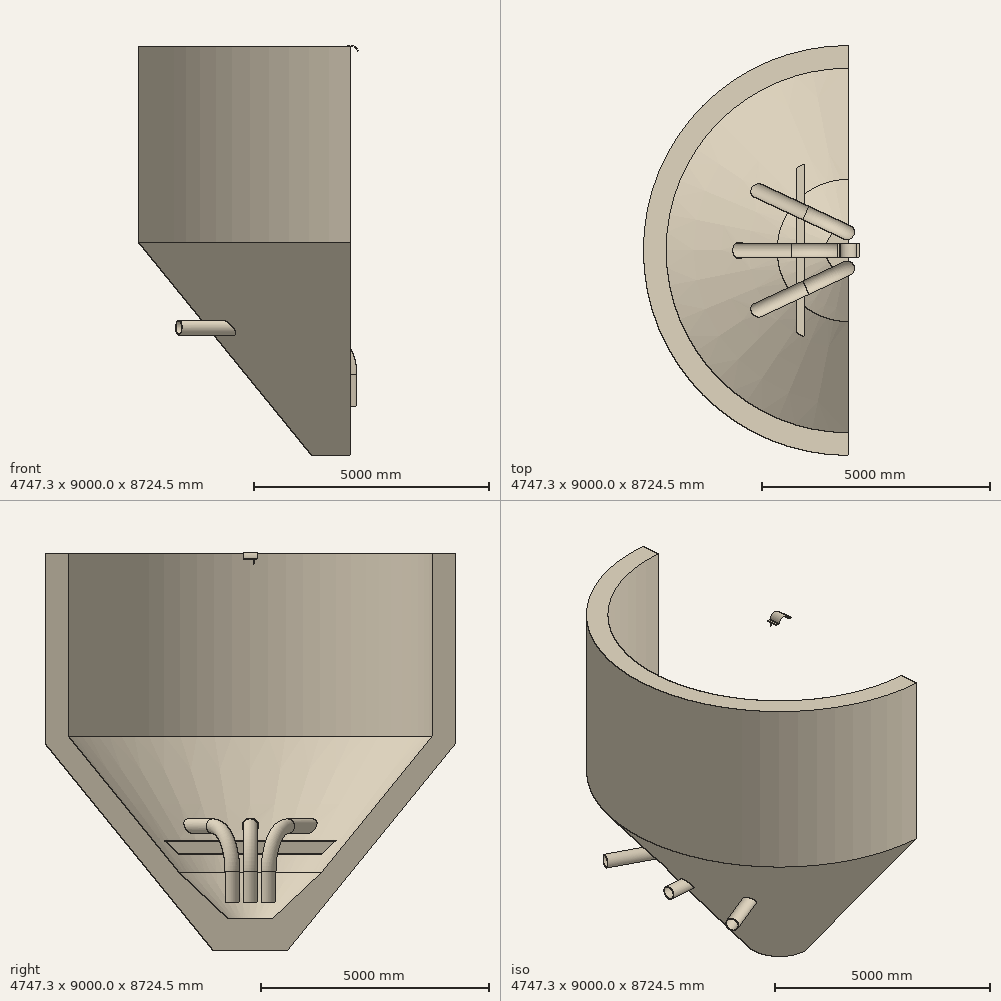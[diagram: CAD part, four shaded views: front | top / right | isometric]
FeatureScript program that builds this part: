
annotation { "Feature Type Name" : "Feature", "Feature Type Description" : "" }
export const myFeature = defineFeature(function(context is Context, id is Id, definition is map)
    precondition{}
    {
        {
            var Q0;
            Q0=qCreatedBy(makeId("Front.planeOp"),FACE);
            var sketch = newSketch(context, id + "F0", { "sketchPlane" : qUnion([Q0])});
            skLineSegment(sketch, "E0", {"start": v(-119.04, 0) * mm, "end": v(208.1, 0) * mm, "construction": true});
            skArc(sketch, "E1", {"start": v(164.9, -41.35) * mm, "mid": v(104.57, -134.03) * mm, "end": v(0, -170) * mm});
            skLineSegment(sketch, "E2", {"start": v(179.44, -30) * mm, "end": v(247.33, -30) * mm});
            skLineSegment(sketch, "E3", {"start": v(0, 1013.15) * mm, "end": v(0, 0) * mm, "construction": true});
            skArc(sketch, "E4.0", {"start": v(171.16, -48.88) * mm, "mid": v(165.4, -65.76) * mm, "end": v(158, -81.98) * mm});
            skLineSegment(sketch, "E5", {"start": v(185.58, -38) * mm, "end": v(247.33, -38) * mm});
            skLineSegment(sketch, "E6", {"start": v(247.33, -30) * mm, "end": v(247.33, -38) * mm});
            skPoint(sketch, "E7.visualSharp", {"position": v(167.33, -30) * mm});
            skArc(sketch, "E7.filletArc", {"start": v(179.44, -30) * mm, "mid": v(170.22, -33.17) * mm, "end": v(164.9, -41.35) * mm});
            skPoint(sketch, "E8.visualSharp", {"position": v(173.9, -38) * mm});
            skArc(sketch, "E8.filletArc", {"start": v(185.58, -38) * mm, "mid": v(176.55, -41.03) * mm, "end": v(171.16, -48.88) * mm});
            skLineSegment(sketch, "E9.MirrorCS", {"start": v(-247.33, -30) * mm, "end": v(-247.33, -38) * mm});
            skArc(sketch, "E10.MirrorCS", {"start": v(-185.58, -38) * mm, "mid": v(-176.55, -41.03) * mm, "end": v(-171.16, -48.88) * mm});
            skArc(sketch, "E11.MirrorCS", {"start": v(-179.44, -30) * mm, "mid": v(-170.22, -33.17) * mm, "end": v(-164.9, -41.35) * mm});
            skArc(sketch, "E12.MirrorCS", {"start": v(-171.16, -48.88) * mm, "mid": v(-165.4, -65.76) * mm, "end": v(-158, -81.98) * mm});
            skLineSegment(sketch, "E13.MirrorCS", {"start": v(-179.44, -30) * mm, "end": v(-247.33, -30) * mm});
            skLineSegment(sketch, "E14.MirrorCS", {"start": v(-185.58, -38) * mm, "end": v(-247.33, -38) * mm});
            skPoint(sketch, "E15.MirrorP", {"position": v(-173.9, -38) * mm});
            skArc(sketch, "E16.MirrorCS", {"start": v(-164.9, -41.35) * mm, "mid": v(-104.57, -134.03) * mm, "end": v(0, -170) * mm});
            skPoint(sketch, "E17.MirrorP", {"position": v(-167.33, -30) * mm});
            skLineSegment(sketch, "E18", {"start": v(158, -81.98) * mm, "end": v(158, -251.98) * mm});
            skLineSegment(sketch, "E19", {"start": v(150, -95.83) * mm, "end": v(150, -251.98) * mm});
            skLineSegment(sketch, "E20.MirrorCS", {"start": v(-158, -81.98) * mm, "end": v(-158, -251.98) * mm});
            skLineSegment(sketch, "E21.MirrorCS", {"start": v(-150, -95.83) * mm, "end": v(-150, -251.98) * mm});
            skArc(sketch, "E22.trimOffspring", {"start": v(150, -95.83) * mm, "mid": v(85.52, -156.11) * mm, "end": v(0, -178) * mm});
            skArc(sketch, "E23.trimOffspring", {"start": v(-150, -95.83) * mm, "mid": v(-85.52, -156.11) * mm, "end": v(0, -178) * mm});
            skLineSegment(sketch, "E24.MirrorCS", {"start": v(-247.33, 30) * mm, "end": v(-247.33, 38) * mm});
            skArc(sketch, "E25.MirrorCS", {"start": v(185.58, 38) * mm, "mid": v(176.55, 41.03) * mm, "end": v(171.16, 48.88) * mm});
            skLineSegment(sketch, "E26.MirrorCS", {"start": v(247.33, 30) * mm, "end": v(247.33, 38) * mm});
            skArc(sketch, "E27.MirrorCS", {"start": v(-179.44, 30) * mm, "mid": v(-170.22, 33.17) * mm, "end": v(-164.9, 41.35) * mm});
            skArc(sketch, "E28.MirrorCS", {"start": v(-185.58, 38) * mm, "mid": v(-176.55, 41.03) * mm, "end": v(-171.16, 48.88) * mm});
            skArc(sketch, "E29.MirrorCS", {"start": v(179.44, 30) * mm, "mid": v(170.22, 33.17) * mm, "end": v(164.9, 41.35) * mm});
            skArc(sketch, "E30.MirrorCS", {"start": v(-171.16, 48.88) * mm, "mid": v(-165.4, 65.76) * mm, "end": v(-158, 81.98) * mm});
            skPoint(sketch, "E31.MirrorP", {"position": v(173.9, 38) * mm});
            skLineSegment(sketch, "E32.MirrorCS", {"start": v(185.58, 38) * mm, "end": v(247.33, 38) * mm});
            skPoint(sketch, "E33.MirrorP", {"position": v(-167.33, 30) * mm});
            skArc(sketch, "E34.MirrorCS", {"start": v(171.16, 48.88) * mm, "mid": v(165.4, 65.76) * mm, "end": v(158, 81.98) * mm});
            skLineSegment(sketch, "E35.MirrorCS", {"start": v(179.44, 30) * mm, "end": v(247.33, 30) * mm});
            skArc(sketch, "E36.MirrorCS", {"start": v(164.9, 41.35) * mm, "mid": v(104.57, 134.03) * mm, "end": v(0, 170) * mm});
            skLineSegment(sketch, "E37.MirrorCS", {"start": v(-179.44, 30) * mm, "end": v(-247.33, 30) * mm});
            skLineSegment(sketch, "E38.MirrorCS", {"start": v(-185.58, 38) * mm, "end": v(-247.33, 38) * mm});
            skArc(sketch, "E39.MirrorCS", {"start": v(-164.9, 41.35) * mm, "mid": v(-104.57, 134.03) * mm, "end": v(0, 170) * mm});
            skArc(sketch, "E40.MirrorCS", {"start": v(158, 81.98) * mm, "mid": v(92.45, 152.11) * mm, "end": v(0, 178) * mm});
            skPoint(sketch, "E41.MirrorP", {"position": v(167.33, 30) * mm});
            skArc(sketch, "E42.MirrorCS", {"start": v(-158, 81.98) * mm, "mid": v(-92.45, 152.11) * mm, "end": v(0, 178) * mm});
            skPoint(sketch, "E43.MirrorP", {"position": v(-173.9, 38) * mm});
            skLineSegment(sketch, "E44", {"start": v(-158, -251.98) * mm, "end": v(-150, -251.98) * mm});
            skLineSegment(sketch, "E45", {"start": v(150, -251.98) * mm, "end": v(158, -251.98) * mm});
            skSolve(sketch);
        }
        {
            var Q0;
            Q0=makeQuery(id+"F0.imprint","IMPRINT",FACE,{"disambiguationData":[TD([[makeQuery(id+"F0.imprint","IMPRINT",EDGE,{"derivedFrom":sQuery(id+"F0.wireOp",EDGE,"E24.MirrorCS")}),-1.0]])]});
            var Q1;
            Q1=makeQuery(id+"F0.imprint","IMPRINT",FACE,{"disambiguationData":[TD([[makeQuery(id+"F0.imprint","IMPRINT",EDGE,{"derivedFrom":sQuery(id+"F0.wireOp",EDGE,"E1")}),1.0]])]});
            extrude(context, id + "F1", {"entities" : qUnion([Q0, Q1]), "depth" : 150 * mm, "offsetDistance" : 25 * mm, "hasSecondDirection" : true, "secondDirectionOppositeDirection" : true, "secondDirectionDepth" : 150 * mm});
        }
        {
            var Q0;
            Q0=qCreatedBy(makeId("Front.planeOp"),FACE);
            var sketch = newSketch(context, id + "F2", { "sketchPlane" : qUnion([Q0])});
            skLineSegment(sketch, "E46", {"start": v(0, 153.5) * mm, "end": v(0, -9846.17) * mm, "construction": true});
            skLineSegment(sketch, "E47", {"start": v(-4500, 153.5) * mm, "end": v(-4517.1, 153.5) * mm});
            skLineSegment(sketch, "E48", {"start": v(-4500, 153.5) * mm, "end": v(-4500, -4024.05) * mm});
            skLineSegment(sketch, "E49", {"start": v(-4500, -4024.05) * mm, "end": v(-824.75, -8546.5) * mm});
            skLineSegment(sketch, "E50", {"start": v(-824.75, -8546.5) * mm, "end": v(0, -8546.5) * mm});
            skLineSegment(sketch, "E51", {"start": v(0, -8546.5) * mm, "end": v(0, -7846.5) * mm});
            skLineSegment(sketch, "E52", {"start": v(0, -7846.5) * mm, "end": v(-500, -7846.5) * mm});
            skLineSegment(sketch, "E53", {"start": v(-500, -7846.5) * mm, "end": v(-1562, -6846.5) * mm});
            skLineSegment(sketch, "E54", {"start": v(-1562, -6846.5) * mm, "end": v(-4000, -3846.5) * mm});
            skLineSegment(sketch, "E55", {"start": v(-4500, 153.5) * mm, "end": v(-4000, 153.5) * mm});
            skLineSegment(sketch, "E56", {"start": v(-4000, 153.5) * mm, "end": v(-4000, -3846.5) * mm});
            skLineSegment(sketch, "E57", {"start": v(0, -5826.5) * mm, "end": v(-3035.2, -5826.5) * mm, "construction": true});
            skLineSegment(sketch, "E58.bottom", {"start": v(-1132.5, -6146.5) * mm, "end": v(-967.5, -6146.5) * mm});
            skLineSegment(sketch, "E58.top", {"start": v(-1132.5, -6453.5) * mm, "end": v(-967.5, -6453.5) * mm});
            skLineSegment(sketch, "E58.left", {"start": v(-1132.5, -6146.5) * mm, "end": v(-1132.5, -6156.7) * mm});
            skLineSegment(sketch, "E58.right", {"start": v(-967.5, -6146.5) * mm, "end": v(-967.5, -6156.7) * mm});
            skLineSegment(sketch, "E59", {"start": v(-1132.5, -6453.5) * mm, "end": v(-967.5, -6146.5) * mm, "construction": true});
            skPoint(sketch, "E60", {"position": v(-1050, -6300) * mm});
            skLineSegment(sketch, "E61", {"start": v(-1132.5, -6156.7) * mm, "end": v(-1064.45, -6156.7) * mm});
            skLineSegment(sketch, "E62", {"start": v(-1132.5, -6443.3) * mm, "end": v(-1064.45, -6443.3) * mm});
            skLineSegment(sketch, "E63", {"start": v(-1053.05, -6168.1) * mm, "end": v(-1053.05, -6431.9) * mm});
            skLineSegment(sketch, "E64", {"start": v(-1046.95, -6168.1) * mm, "end": v(-1046.95, -6431.9) * mm});
            skLineSegment(sketch, "E65.trimOffspring", {"start": v(-1035.55, -6443.3) * mm, "end": v(-967.5, -6443.3) * mm});
            skLineSegment(sketch, "E66.trimOffspring", {"start": v(-1035.55, -6156.7) * mm, "end": v(-967.5, -6156.7) * mm});
            skLineSegment(sketch, "E67.trimOffspring", {"start": v(-967.5, -6443.3) * mm, "end": v(-967.5, -6453.5) * mm});
            skLineSegment(sketch, "E68.trimOffspring", {"start": v(-1132.5, -6443.3) * mm, "end": v(-1132.5, -6453.5) * mm});
            skLineSegment(sketch, "E69", {"start": v(-1053.05, -6300) * mm, "end": v(-1046.95, -6300) * mm, "construction": true});
            skPoint(sketch, "E70.visualSharp", {"position": v(-1053.05, -6156.7) * mm});
            skArc(sketch, "E70.filletArc", {"start": v(-1053.05, -6168.1) * mm, "mid": v(-1056.39, -6160.04) * mm, "end": v(-1064.45, -6156.7) * mm});
            skPoint(sketch, "E71.visualSharp", {"position": v(-1046.95, -6156.7) * mm});
            skArc(sketch, "E71.filletArc", {"start": v(-1035.55, -6156.7) * mm, "mid": v(-1043.61, -6160.04) * mm, "end": v(-1046.95, -6168.1) * mm});
            skPoint(sketch, "E72.visualSharp", {"position": v(-1053.05, -6443.3) * mm});
            skArc(sketch, "E72.filletArc", {"start": v(-1064.45, -6443.3) * mm, "mid": v(-1056.39, -6439.96) * mm, "end": v(-1053.05, -6431.9) * mm});
            skPoint(sketch, "E73.visualSharp", {"position": v(-1046.95, -6443.3) * mm});
            skArc(sketch, "E73.filletArc", {"start": v(-1046.95, -6431.9) * mm, "mid": v(-1043.61, -6439.96) * mm, "end": v(-1035.55, -6443.3) * mm});
            skSolve(sketch);
        }
        {
            var Q0;
            Q0=makeQuery(id+"F2.imprint","IMPRINT",FACE,{"disambiguationData":[TD([[makeQuery(id+"F2.imprint","IMPRINT",EDGE,{"derivedFrom":sQuery(id+"F2.wireOp",EDGE,"E48")}),1.0]])]});
            var Q1;
            Q1=sQuery(id+"F2.wireOp",EDGE,"E46");
            revolve(context, id + "F3", {"surfaceOperationType" : NewSurfaceOperationType.NEW, "entities" : qUnion([Q0]), "axis" : qUnion([Q1]), "revolveType" : RevolveType.SYMMETRIC, "angle" : 180 * degree});
        }
        {
            var Q0;
            Q0=makeQuery(id+"F2.imprint","IMPRINT",FACE,{"disambiguationData":[TD([[makeQuery(id+"F2.imprint","IMPRINT",EDGE,{"derivedFrom":sQuery(id+"F2.wireOp",EDGE,"E58.bottom")}),-1.0]])]});
            extrude(context, id + "F4", {"entities" : qUnion([Q0]), "operationType" : NewBodyOperationType.ADD, "depth" : 2000 * mm, "offsetDistance" : 25 * mm, "hasSecondDirection" : true, "secondDirectionOppositeDirection" : true, "secondDirectionDepth" : 2000 * mm});
        }
        {
            var Q0;
            Q0=makeQuery(id+"F3.opRevolve","SWEPT_FACE",FACE,{"disambiguationData":[OSD([sQuery(id+"F2.wireOp",EDGE,"E52")])]});
            cPlane(context, id + "F5", {"entities" : qUnion([Q0]), "cplaneType" : CPlaneType.OFFSET, "offset" : 2020 * mm, "width" : 150 * mm, "height" : 150 * mm});
        }
        {
            var Q0;
            Q0=qCreatedBy(id+"F5.planeOp",FACE);
            var sketch = newSketch(context, id + "F6", { "sketchPlane" : qUnion([Q0])});
            skLineSegment(sketch, "E74", {"start": v(0, 0) * mm, "end": v(-3650, 0) * mm, "construction": true});
            skLineSegment(sketch, "E75", {"start": v(-3650, -2088.2) * mm, "end": v(828.17, 0) * mm, "construction": true});
            skLineSegment(sketch, "E76", {"start": v(-3650, 2088.2) * mm, "end": v(828.17, 0) * mm, "construction": true});
            skLineSegment(sketch, "E77", {"start": v(0, 0) * mm, "end": v(828.17, 0) * mm, "construction": true});
            skSolve(sketch);
        }
        {
            var Q0;
            Q0=sQuery(id+"F6.wireOp",VERTEX,"E75.start");
            var Q1;
            Q1=sQuery(id+"F6.wireOp",EDGE,"E75");
            cPlane(context, id + "F7", {"entities" : qUnion([Q0, Q1]), "cplaneType" : CPlaneType.LINE_POINT, "offset" : 25 * mm, "width" : 150 * mm, "height" : 150 * mm});
        }
        {
            var Q0;
            Q0=sQuery(id+"F6.wireOp",VERTEX,"E76.start");
            var Q1;
            Q1=sQuery(id+"F6.wireOp",EDGE,"E76");
            cPlane(context, id + "F8", {"entities" : qUnion([Q0, Q1]), "cplaneType" : CPlaneType.LINE_POINT, "offset" : 25 * mm, "width" : 150 * mm, "height" : 150 * mm});
        }
        {
            var Q0;
            Q0=sQuery(id+"F6.wireOp",VERTEX,"E74.end");
            var Q1;
            Q1=sQuery(id+"F6.wireOp",EDGE,"E74");
            cPlane(context, id + "F9", {"entities" : qUnion([Q0, Q1]), "cplaneType" : CPlaneType.LINE_POINT, "offset" : 25 * mm, "width" : 150 * mm, "height" : 150 * mm});
        }
        {
            var Q0;
            Q0=qCreatedBy(id+"F8.planeOp",FACE);
            var sketch = newSketch(context, id + "F10", { "sketchPlane" : qUnion([Q0])});
            skPoint(sketch, "E78.0", {"position": v(350, -5826.5) * mm});
            skCircle(sketch, "E79", {"center": v(350, -5826.5) * mm, "radius": 161.95 * mm});
            skCircle(sketch, "E80.0", {"center": v(350, -5826.5) * mm, "radius": 141.95 * mm});
            skSolve(sketch);
        }
        {
            var Q0;
            Q0=qCreatedBy(id+"F9.planeOp",FACE);
            var sketch = newSketch(context, id + "F11", { "sketchPlane" : qUnion([Q0])});
            skPoint(sketch, "E81.0", {"position": v(0, -5826.5) * mm});
            skCircle(sketch, "E82", {"center": v(0, -5826.5) * mm, "radius": 161.95 * mm});
            skCircle(sketch, "E83.0", {"center": v(0, -5826.5) * mm, "radius": 141.95 * mm});
            skCircle(sketch, "E84.0", {"center": v(0, -5826.5) * mm, "radius": 181.95 * mm});
            skSolve(sketch);
        }
        {
            var Q0;
            Q0=qCreatedBy(id+"F7.planeOp",FACE);
            var sketch = newSketch(context, id + "F12", { "sketchPlane" : qUnion([Q0])});
            skPoint(sketch, "E85.0", {"position": v(-350, -5826.5) * mm});
            skCircle(sketch, "E86", {"center": v(-350, -5826.5) * mm, "radius": 161.95 * mm});
            skCircle(sketch, "E87.0", {"center": v(-350, -5826.5) * mm, "radius": 141.95 * mm});
            skSolve(sketch);
        }
        {
            var Q0;
            Q0=makeQuery(id+"F1.opExtrude","SWEPT_FACE",FACE,{"disambiguationData":[OSD([sQuery(id+"F0.wireOp",EDGE,"E38.MirrorCS")])]});
            var sketch = newSketch(context, id + "F13", { "sketchPlane" : qUnion([Q0])});
            skLineSegment(sketch, "E88.0", {"start": v(-247.33, -150) * mm, "end": v(-247.33, 150) * mm, "construction": true});
            skLineSegment(sketch, "E88.1", {"start": v(-185.58, -150) * mm, "end": v(-247.33, -150) * mm, "construction": true});
            skLineSegment(sketch, "E88.2", {"start": v(-185.58, -150) * mm, "end": v(-185.58, 150) * mm, "construction": true});
            skLineSegment(sketch, "E88.3", {"start": v(-185.58, 150) * mm, "end": v(-247.33, 150) * mm, "construction": true});
            skLineSegment(sketch, "E89", {"start": v(-216.46, 150) * mm, "end": v(-216.46, -150) * mm, "construction": true});
            skPoint(sketch, "E90", {"position": v(-216.46, 75) * mm});
            skCircle(sketch, "E91", {"center": v(-216.46, 75) * mm, "radius": 10 * mm});
            skSolve(sketch);
        }
        {
            var Q0;
            Q0 = qSketchRegion(id + "F13", true);
            extrude(context, id + "F14", {"entities" : qUnion([Q0]), "operationType" : NewBodyOperationType.ADD, "oppositeDirection" : true, "depth" : 120 * mm, "offsetDistance" : 25 * mm, "hasSecondDirection" : true, "secondDirectionOppositeDirection" : false, "secondDirectionDepth" : 1 * mm});
        }
        {
            var Q0;
            Q0=makeQuery(id+"F11.imprint","IMPRINT",FACE,{"disambiguationData":[TD([[makeQuery(id+"F11.imprint","IMPRINT",EDGE,{"derivedFrom":sQuery(id+"F11.wireOp",EDGE,"E82")}),-1.0]])]});
            var Q1;
            Q1=sQuery(id+"F11.wireOp",EDGE,"E84.0");
            var Q2;
            Q2=sQuery(id+"F11.wireOp",EDGE,"E82");
            extrude(context, id + "F15", {"entities" : qUnion([Q0]), "operationType" : NewBodyOperationType.REMOVE, "surfaceEntities" : qUnion([Q1, Q2]), "oppositeDirection" : true, "depth" : 2000 * mm, "offsetDistance" : 25 * mm});
        }
        {
            var Q0;
            Q0=sQuery(id+"F6.wireOp",EDGE,"E76");
            cPlane(context, id + "F16", {"entities" : qUnion([Q0]), "cplaneType" : CPlaneType.LINE_ANGLE, "offset" : 25 * mm, "angle" : 0 * degree, "width" : 150 * mm, "height" : 150 * mm});
        }
        {
            var Q0;
            Q0=sQuery(id+"F6.wireOp",EDGE,"E74");
            cPlane(context, id + "F17", {"entities" : qUnion([Q0]), "cplaneType" : CPlaneType.LINE_ANGLE, "offset" : 25 * mm, "angle" : 0 * degree, "width" : 150 * mm, "height" : 150 * mm});
        }
        {
            var Q0;
            Q0=sQuery(id+"F6.wireOp",EDGE,"E75");
            cPlane(context, id + "F18", {"entities" : qUnion([Q0]), "cplaneType" : CPlaneType.LINE_ANGLE, "offset" : 25 * mm, "angle" : 0 * degree, "width" : 150 * mm, "height" : 150 * mm});
        }
        {
            var Q0;
            Q0=qCreatedBy(id+"F17.planeOp",FACE);
            var sketch = newSketch(context, id + "F19", { "sketchPlane" : qUnion([Q0])});
            skLineSegment(sketch, "E92.0", {"start": v(-1250, -5826.5) * mm, "end": v(-3650, -5826.5) * mm});
            skLineSegment(sketch, "E93", {"start": v(-250, -6826.5) * mm, "end": v(-250, -7496.5) * mm});
            skPoint(sketch, "E94.newPointB", {"position": v(-250, -5826.5) * mm});
            skArc(sketch, "E94.filletArc", {"start": v(-250, -6826.5) * mm, "mid": v(-542.9, -6119.4) * mm, "end": v(-1250, -5826.5) * mm});
            skSolve(sketch);
        }
        {
            var Q0;
            Q0=makeQuery(id+"F11.imprint","IMPRINT",FACE,{"disambiguationData":[TD([[makeQuery(id+"F11.imprint","IMPRINT",EDGE,{"derivedFrom":sQuery(id+"F11.wireOp",EDGE,"E82")}),1.0]])]});
            var Q1;
            Q1 = qConstructionFilter(qBodyType(qCreatedBy(id + "F19" ,EDGE), BodyType.WIRE), ConstructionObject.NO);
            sweep(context, id + "F20", {"operationType" : NewBodyOperationType.ADD, "profiles" : qUnion([Q0]), "path" : qUnion([Q1])});
        }
        {
            var Q0;
            Q0=qCreatedBy(id+"F18.planeOp",FACE);
            var sketch = newSketch(context, id + "F21", { "sketchPlane" : qUnion([Q0])});
            skLineSegment(sketch, "E95.0", {"start": v(4190.54, -5826.5) * mm, "end": v(1190.54, -5826.5) * mm});
            skLineSegment(sketch, "E96", {"start": v(190.54, -6826.5) * mm, "end": v(190.54, -7496.5) * mm});
            skPoint(sketch, "E97.newPointA", {"position": v(-750.58, -5826.5) * mm});
            skPoint(sketch, "E97.newPointB", {"position": v(190.54, -5826.5) * mm});
            skArc(sketch, "E97.filletArc", {"start": v(1190.54, -5826.5) * mm, "mid": v(483.43, -6119.4) * mm, "end": v(190.54, -6826.5) * mm});
            skSolve(sketch);
        }
        {
            var Q0;
            Q0=makeQuery(id+"F12.imprint","IMPRINT",FACE,{"disambiguationData":[TD([[makeQuery(id+"F12.imprint","IMPRINT",EDGE,{"derivedFrom":sQuery(id+"F12.wireOp",EDGE,"E86")}),1.0]])]});
            var Q1;
            Q1 = qConstructionFilter(qBodyType(qCreatedBy(id + "F21" ,EDGE), BodyType.WIRE), ConstructionObject.NO);
            sweep(context, id + "F22", {"operationType" : NewBodyOperationType.ADD, "profiles" : qUnion([Q0]), "path" : qUnion([Q1])});
        }
        {
            var Q0;
            Q0=qCreatedBy(id+"F16.planeOp",FACE);
            var sketch = newSketch(context, id + "F23", { "sketchPlane" : qUnion([Q0])});
            skLineSegment(sketch, "E98.0", {"start": v(4190.54, -5826.5) * mm, "end": v(1190.54, -5826.5) * mm});
            skLineSegment(sketch, "E99", {"start": v(190.54, -6826.5) * mm, "end": v(190.54, -7496.5) * mm});
            skPoint(sketch, "E100.visualSharp", {"position": v(190.54, -5826.5) * mm});
            skArc(sketch, "E100.filletArc", {"start": v(1190.54, -5826.5) * mm, "mid": v(483.43, -6119.4) * mm, "end": v(190.54, -6826.5) * mm});
            skSolve(sketch);
        }
        {
            var Q0;
            Q0=makeQuery(id+"F10.imprint","IMPRINT",FACE,{"disambiguationData":[TD([[makeQuery(id+"F10.imprint","IMPRINT",EDGE,{"derivedFrom":sQuery(id+"F10.wireOp",EDGE,"E79")}),1.0]])]});
            var Q1;
            Q1 = qConstructionFilter(qBodyType(qCreatedBy(id + "F23" ,EDGE), BodyType.WIRE), ConstructionObject.NO);
            sweep(context, id + "F24", {"operationType" : NewBodyOperationType.ADD, "profiles" : qUnion([Q0]), "path" : qUnion([Q1])});
        }
    });
